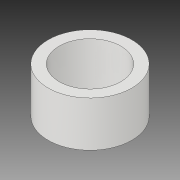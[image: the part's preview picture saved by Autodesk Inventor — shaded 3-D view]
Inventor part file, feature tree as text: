
AUTODESK INVENTOR PART (.ipt)
format: ipt  version: 2018 (Build 220112000, 112)  size: 100,352 bytes
history: native  units: in
note: dims shown in document units (in); Inventor stores cm internally (conversion verified against a paired STEP export)
features: extrude x2, sketch x2
ambient origin geometry x8: Origin, YZ Plane, XZ Plane, XY Plane, X Axis, Y Axis, Z Axis, Center Point
bodies: Solid1 (feature_tree)
feature tree (4):
  extrude  "Extrusion1"  Depth=0.28in TaperAngle=0.0deg
  extrude  "Extrusion2"  Depth=0.345in TaperAngle=0.0deg
  sketch  "Sketch1"  dims[d0=0.518in d1=0.28in d2=0.0in]
  sketch  "Sketch2"  dims[d3=0.382in d4=0.345in d5=0.0in]
